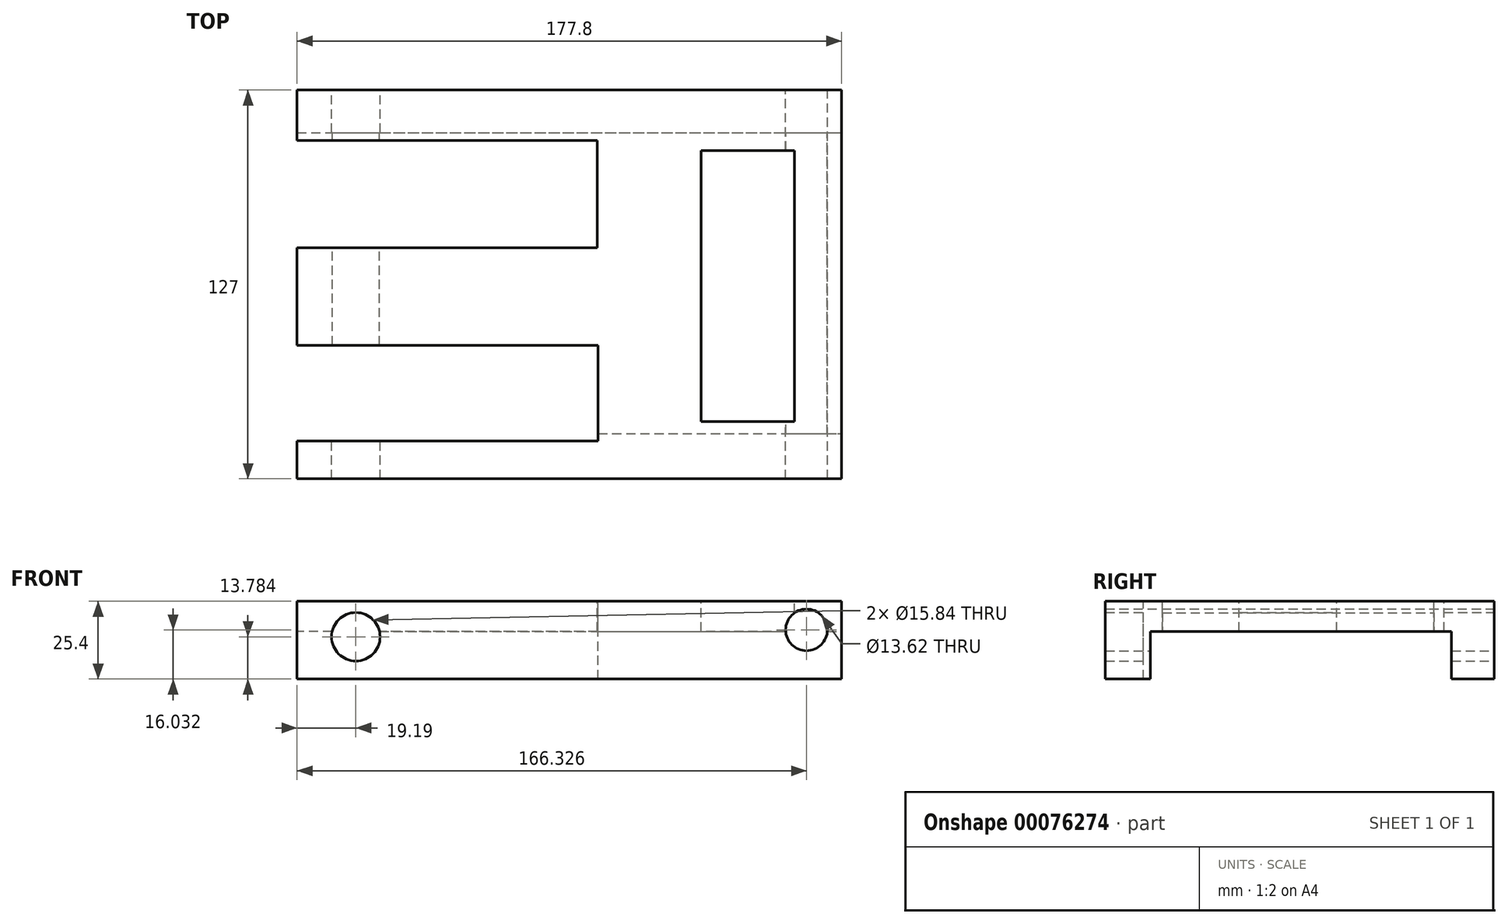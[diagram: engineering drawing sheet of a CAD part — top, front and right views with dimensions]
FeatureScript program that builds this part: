
annotation { "Feature Type Name" : "Feature", "Feature Type Description" : "" }
export const myFeature = defineFeature(function(context is Context, id is Id, definition is map)
    precondition{}
    {
        {
            var Q0;
            Q0=qCreatedBy(makeId("Right.planeOp"),FACE);
            var sketch = newSketch(context, id + "F0", { "sketchPlane" : qUnion([Q0])});
            skLineSegment(sketch, "E0.bottom", {"start": v(-56.15, 25.4) * mm, "end": v(70.85, 25.4) * mm});
            skLineSegment(sketch, "E0.top", {"start": v(-56.15, 0) * mm, "end": v(70.85, 0) * mm});
            skLineSegment(sketch, "E0.left", {"start": v(-56.15, 25.4) * mm, "end": v(-56.15, 0) * mm});
            skLineSegment(sketch, "E0.right", {"start": v(70.85, 25.4) * mm, "end": v(70.85, 0) * mm});
            skSolve(sketch);
        }
        {
            var Q0;
            Q0=makeQuery(id+"F0.imprint","IMPRINT",FACE,{"disambiguationData":[TD([[makeQuery(id+"F0.imprint","IMPRINT",EDGE,{"derivedFrom":sQuery(id+"F0.wireOp",EDGE,"E0.bottom")}),-1.0]])]});
            extrude(context, id + "F1", {"entities" : qUnion([Q0]), "depth" : 152.4 * mm});
        }
        {
            var Q0;
            Q0=makeQuery(id+"F1.opExtrude","CAP_FACE",FACE,{"disambiguationData":[OSD([sQuery(id+"F0.wireOp",EDGE,"E0.bottom"),sQuery(id+"F0.wireOp",EDGE,"E0.top"),sQuery(id+"F0.wireOp",EDGE,"E0.left"),sQuery(id+"F0.wireOp",EDGE,"E0.right")])],"isStart":false});
            var sketch = newSketch(context, id + "F2", { "sketchPlane" : qUnion([Q0])});
            skLineSegment(sketch, "E1.bottom", {"start": v(-41.42, 15.5) * mm, "end": v(56.92, 15.5) * mm});
            skLineSegment(sketch, "E1.top", {"start": v(-41.42, 0) * mm, "end": v(56.92, 0) * mm});
            skLineSegment(sketch, "E1.left", {"start": v(-41.42, 15.5) * mm, "end": v(-41.42, 0) * mm});
            skLineSegment(sketch, "E1.right", {"start": v(56.92, 15.5) * mm, "end": v(56.92, 0) * mm});
            skSolve(sketch);
        }
        {
            var Q0;
            Q0=makeQuery(id+"F2.imprint","IMPRINT",FACE,{"disambiguationData":[TD([[makeQuery(id+"F2.imprint","IMPRINT",EDGE,{"derivedFrom":sQuery(id+"F2.wireOp",EDGE,"E1.bottom")}),-1.0]])]});
            extrude(context, id + "F3", {"entities" : qUnion([Q0]), "operationType" : NewBodyOperationType.REMOVE, "endBound" : BoundingType.THROUGH_ALL, "oppositeDirection" : true, "depth" : 25.4 * mm});
        }
        {
            var Q0;
            Q0=makeQuery(id+"F1.opExtrude","CAP_FACE",FACE,{"disambiguationData":[OSD([sQuery(id+"F0.wireOp",EDGE,"E0.bottom"),sQuery(id+"F0.wireOp",EDGE,"E0.top"),sQuery(id+"F0.wireOp",EDGE,"E0.left"),sQuery(id+"F0.wireOp",EDGE,"E0.right")])],"isStart":false});
            var sketch = newSketch(context, id + "F4", { "sketchPlane" : qUnion([Q0])});
            skSolve(sketch);
        }
        {
            var Q0;
            {var subQ3=sQuery(id+"F0.wireOp",EDGE,"E0.bottom");Q0=makeQuery(id+"F4.imprint","IMPRINT",FACE,{"disambiguationData":[TD([[makeQuery(id+"F4.imprint","IMPRINT",EDGE,{"derivedFrom":makeQuery(id+"F1.opExtrude","CAP_EDGE",EDGE,{"disambiguationData":[OSD([subQ3])],"isStart":false})}),-1.0]])]});}
            extrude(context, id + "F5", {"entities" : qUnion([Q0]), "operationType" : NewBodyOperationType.ADD, "depth" : 25.4 * mm});
        }
        {
            var Q0;
            {var subQ0=sQuery(id+"F0.wireOp",EDGE,"E0.right");Q0=makeQuery(id+"F5.boolean.opBoolean","MERGE",FACE,{"derivedFrom":[makeQuery(id+"F1.opExtrude","SWEPT_FACE",FACE,{"disambiguationData":[OSD([subQ0])]}),makeQuery(id+"F5.opExtrude","SWEPT_FACE",FACE,{"disambiguationData":[OSD([subQ0])]})]});}
            var sketch = newSketch(context, id + "F6", { "sketchPlane" : qUnion([Q0])});
            skCircle(sketch, "E2", {"center": v(-166.33, 16.03) * mm, "radius": 6.81 * mm});
            skSolve(sketch);
        }
        {
            var Q0;
            Q0=makeQuery(id+"F6.imprint","IMPRINT",FACE,{"disambiguationData":[TD([[makeQuery(id+"F6.imprint","IMPRINT",EDGE,{"derivedFrom":sQuery(id+"F6.wireOp",EDGE,"E2")}),1.0]])]});
            extrude(context, id + "F7", {"entities" : qUnion([Q0]), "operationType" : NewBodyOperationType.REMOVE, "endBound" : BoundingType.THROUGH_ALL, "oppositeDirection" : true, "depth" : 25.4 * mm});
        }
        {
            var Q0;
            {var subQ0=sQuery(id+"F0.wireOp",EDGE,"E0.right");Q0=makeQuery(id+"F5.boolean.opBoolean","MERGE",FACE,{"derivedFrom":[makeQuery(id+"F1.opExtrude","SWEPT_FACE",FACE,{"disambiguationData":[OSD([subQ0])]}),makeQuery(id+"F5.opExtrude","SWEPT_FACE",FACE,{"disambiguationData":[OSD([subQ0])]})]});}
            var sketch = newSketch(context, id + "F8", { "sketchPlane" : qUnion([Q0])});
            skSolve(sketch);
        }
        {
            var Q0;
            {var subQ0=sQuery(id+"F0.wireOp",EDGE,"E0.right");Q0=makeQuery(id+"F8.imprint","IMPRINT",FACE,{"disambiguationData":[TD([[makeQuery(id+"F8.imprint","IMPRINT",EDGE,{"derivedFrom":makeQuery(id+"F1.opExtrude","CAP_EDGE",EDGE,{"disambiguationData":[OSD([subQ0])],"isStart":true})}),-1.0]])]});}
            var sketch = newSketch(context, id + "F9", { "sketchPlane" : qUnion([Q0])});
            skSolve(sketch);
        }
        {
            var Q0;
            {var subQ0=sQuery(id+"F0.wireOp",EDGE,"E0.right");Q0=makeQuery(id+"F9.imprint","IMPRINT",FACE,{"disambiguationData":[TD([[makeQuery(id+"F9.imprint","IMPRINT",EDGE,{"derivedFrom":makeQuery(id+"F8.imprint","IMPRINT",EDGE,{"derivedFrom":makeQuery(id+"F1.opExtrude","CAP_EDGE",EDGE,{"disambiguationData":[OSD([subQ0])],"isStart":true})})}),-1.0]])]});}
            var sketch = newSketch(context, id + "F10", { "sketchPlane" : qUnion([Q0])});
            skCircle(sketch, "E3", {"center": v(-19.2, 13.78) * mm, "radius": 7.92 * mm});
            skPoint(sketch, "E3.first.point", {"position": v(-27.08, 14.49) * mm});
            skPoint(sketch, "E3.second.point", {"position": v(-11.3, 14.47) * mm});
            skPoint(sketch, "E3.third.point", {"position": v(-22.74, 20.86) * mm});
            skSolve(sketch);
        }
        {
            var Q0;
            Q0=makeQuery(id+"F10.imprint","IMPRINT",FACE,{"disambiguationData":[TD([[makeQuery(id+"F10.imprint","IMPRINT",EDGE,{"derivedFrom":sQuery(id+"F10.wireOp",EDGE,"E3")}),1.0]])]});
            extrude(context, id + "F11", {"entities" : qUnion([Q0]), "operationType" : NewBodyOperationType.REMOVE, "endBound" : BoundingType.THROUGH_ALL, "oppositeDirection" : true, "depth" : 25.4 * mm});
        }
        {
            var Q0;
            {var subQ0=sQuery(id+"F0.wireOp",EDGE,"E0.bottom");Q0=makeQuery(id+"F5.boolean.opBoolean","MERGE",FACE,{"derivedFrom":[makeQuery(id+"F1.opExtrude","SWEPT_FACE",FACE,{"disambiguationData":[OSD([subQ0])]}),makeQuery(id+"F5.opExtrude","SWEPT_FACE",FACE,{"disambiguationData":[OSD([subQ0])]})]});}
            var sketch = newSketch(context, id + "F12", { "sketchPlane" : qUnion([Q0])});
            skLineSegment(sketch, "E4.bottom", {"start": v(0, -43.77) * mm, "end": v(98.28, -43.77) * mm});
            skLineSegment(sketch, "E4.top", {"start": v(0, -12.52) * mm, "end": v(98.28, -12.52) * mm});
            skLineSegment(sketch, "E4.left", {"start": v(0, -43.77) * mm, "end": v(0, -12.52) * mm});
            skLineSegment(sketch, "E4.right", {"start": v(98.28, -43.77) * mm, "end": v(98.28, -12.52) * mm});
            skSolve(sketch);
        }
        {
            var Q0;
            Q0=makeQuery(id+"F12.imprint","IMPRINT",FACE,{"disambiguationData":[TD([[makeQuery(id+"F12.imprint","IMPRINT",EDGE,{"derivedFrom":sQuery(id+"F12.wireOp",EDGE,"E4.bottom")}),1.0]])]});
            extrude(context, id + "F13", {"entities" : qUnion([Q0]), "operationType" : NewBodyOperationType.REMOVE, "endBound" : BoundingType.THROUGH_ALL, "oppositeDirection" : true, "depth" : 25.4 * mm});
        }
        {
            var Q0;
            {var subQ0=sQuery(id+"F0.wireOp",EDGE,"E0.bottom");Q0=makeQuery(id+"F5.boolean.opBoolean","MERGE",FACE,{"derivedFrom":[makeQuery(id+"F1.opExtrude","SWEPT_FACE",FACE,{"disambiguationData":[OSD([subQ0])]}),makeQuery(id+"F5.opExtrude","SWEPT_FACE",FACE,{"disambiguationData":[OSD([subQ0])]})]});}
            var sketch = newSketch(context, id + "F14", { "sketchPlane" : qUnion([Q0])});
            skLineSegment(sketch, "E5.bottom", {"start": v(0, 19.36) * mm, "end": v(98.03, 19.36) * mm});
            skLineSegment(sketch, "E5.top", {"start": v(0, 54.42) * mm, "end": v(98.03, 54.42) * mm});
            skLineSegment(sketch, "E5.left", {"start": v(0, 19.36) * mm, "end": v(0, 54.42) * mm});
            skLineSegment(sketch, "E5.right", {"start": v(98.03, 19.36) * mm, "end": v(98.03, 54.42) * mm});
            skSolve(sketch);
        }
        {
            var Q0;
            Q0=makeQuery(id+"F14.imprint","IMPRINT",FACE,{"disambiguationData":[TD([[makeQuery(id+"F14.imprint","IMPRINT",EDGE,{"derivedFrom":sQuery(id+"F14.wireOp",EDGE,"E5.bottom")}),1.0]])]});
            extrude(context, id + "F15", {"entities" : qUnion([Q0]), "operationType" : NewBodyOperationType.REMOVE, "endBound" : BoundingType.THROUGH_ALL, "oppositeDirection" : true, "depth" : 25.4 * mm});
        }
        {
            var Q0;
            {var subQ0=sQuery(id+"F0.wireOp",EDGE,"E0.bottom");Q0=makeQuery(id+"F5.boolean.opBoolean","MERGE",FACE,{"derivedFrom":[makeQuery(id+"F1.opExtrude","SWEPT_FACE",FACE,{"disambiguationData":[OSD([subQ0])]}),makeQuery(id+"F5.opExtrude","SWEPT_FACE",FACE,{"disambiguationData":[OSD([subQ0])]})]});}
            var sketch = newSketch(context, id + "F16", { "sketchPlane" : qUnion([Q0])});
            skLineSegment(sketch, "E6.bottom", {"start": v(131.96, -37.48) * mm, "end": v(162.45, -37.48) * mm});
            skLineSegment(sketch, "E6.top", {"start": v(131.96, 51.1) * mm, "end": v(162.45, 51.1) * mm});
            skLineSegment(sketch, "E6.left", {"start": v(131.96, -37.48) * mm, "end": v(131.96, 51.1) * mm});
            skLineSegment(sketch, "E6.right", {"start": v(162.45, -37.48) * mm, "end": v(162.45, 51.1) * mm});
            skSolve(sketch);
        }
        {
            var Q0;
            Q0=makeQuery(id+"F16.imprint","IMPRINT",FACE,{"disambiguationData":[TD([[makeQuery(id+"F16.imprint","IMPRINT",EDGE,{"derivedFrom":sQuery(id+"F16.wireOp",EDGE,"E6.bottom")}),1.0]])]});
            extrude(context, id + "F17", {"entities" : qUnion([Q0]), "operationType" : NewBodyOperationType.REMOVE, "endBound" : BoundingType.THROUGH_ALL, "oppositeDirection" : true, "depth" : 25.4 * mm});
        }
    });
